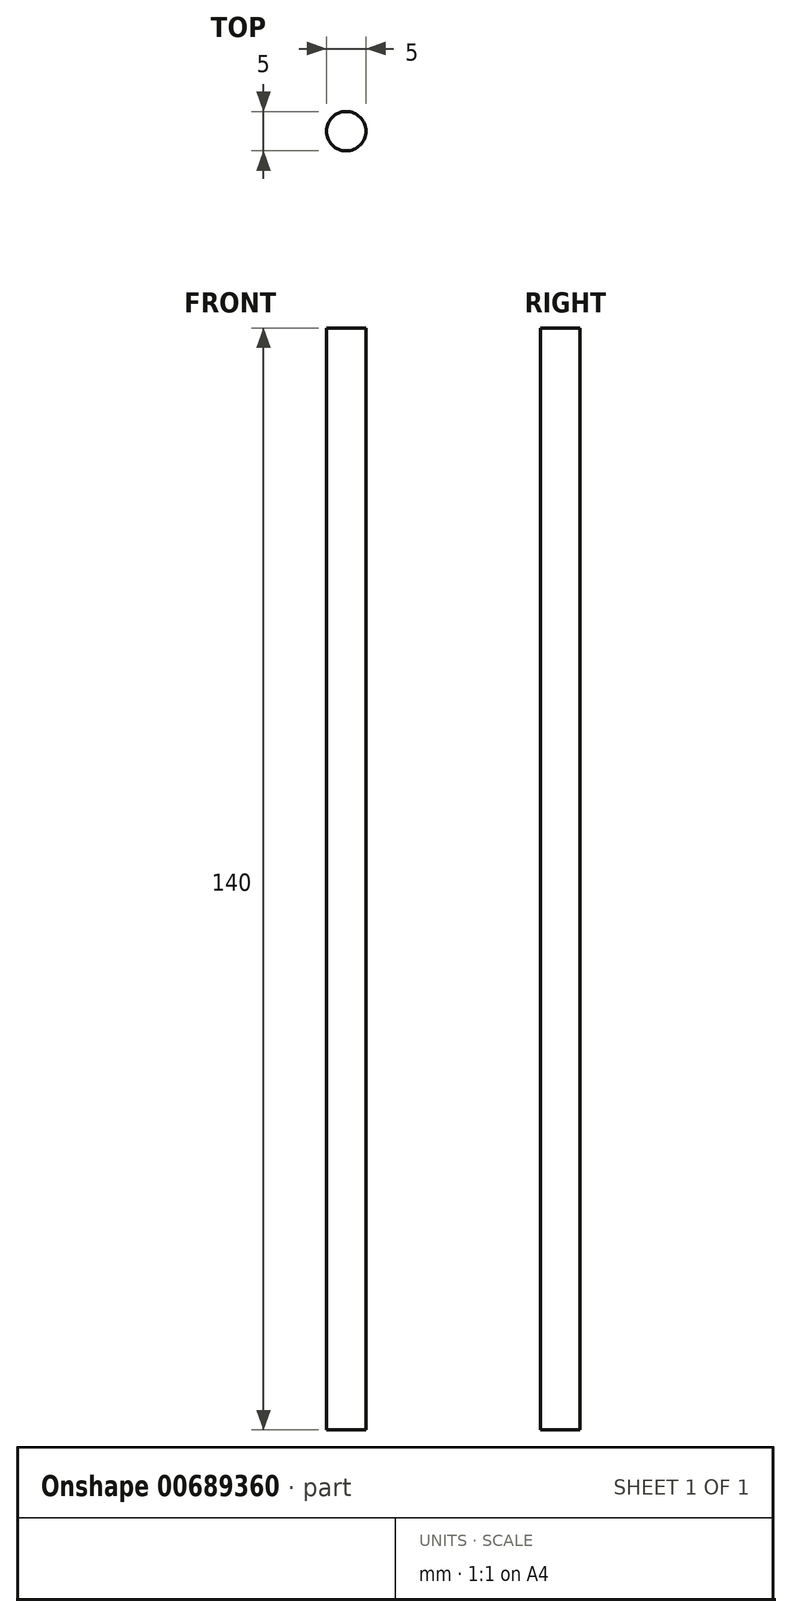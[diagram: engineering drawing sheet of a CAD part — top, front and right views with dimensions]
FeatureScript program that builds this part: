
annotation { "Feature Type Name" : "Feature", "Feature Type Description" : "" }
export const myFeature = defineFeature(function(context is Context, id is Id, definition is map)
    precondition{}
    {
        {
            var Q0;
            Q0=qCreatedBy(makeId("Top.planeOp"),FACE);
            var sketch = newSketch(context, id + "F0", { "sketchPlane" : qUnion([Q0])});
            skCircle(sketch, "E0", {"center": v(0, 0) * mm, "radius": 2.5 * mm});
            skSolve(sketch);
        }
        {
            var Q0;
            Q0=qSketchRegion(id+"F0",true);
            extrude(context, id + "F1", {"entities" : qUnion([Q0]), "depth" : 140 * mm, "offsetDistance" : 25 * mm});
        }
    });
